# Revit family: Grohe_TowelHolder_Selection_41219KF0
name_source: partatom
category: Plumbing Fixtures
units: mm (PartAtom-declared; Revit-internal decimal feet)

## family parameters
Cut with Voids When Loaded = No
Host = Face
OmniClass Number = 23.45.05.00
OmniClass Title = Sanitary Equipment
Part Type = Normal
Room Calculation Point = No
Round Connector Dimension = Use Diameter
Shared = No

## types (1)
- SELECTION Towel Holder (41219KF0)
    Assembly Code = D2010
    AssetType = Fixed
    BIMObjectName = Grohe_TowelHolder_Selection_41219KF0
    CO2NeutralProduction = GROHE is one of the first leading manufacturer within the sanitary industry having a CO2-neutral production.
    CW Connection = No
    ClassificationName = Uniclass2015
    ClassificationValue = Pr_40_20_76_90
    Color = Matt Black
    Cost = 0 $
    Default Elevation = 0 mm  [stored 0 ft]
    Description = SELECTION Towel Holder
    DimensionsDocumentLink = https://cdn.cloud.grohe.com
    DocumentationCertificates = https://www.bimstore.co
    DocumentationInstallationGuide = https://www.bimstore.co
    DocumentationLiterature = https://www.bimstore.co
    DocumentationMaintenance = https://www.bimstore.co
    DocumentationTechnical = https://www.bimstore.co
    DurationUnit = Years
    EF000003 = Wall
    EF000007 = Black
    EF000040 = 30 mm  [stored 0.0984252 ft]
    EF000049 = 441 mm  [stored 1.44685 ft]
    EF000051 = Rack/bracket
    EF000139 = Lacquered
    EF000301 = TRUE
    EF000329 = FALSE
    EF000551 = 0 mm  [stored 0 ft]
    EF001438 = 0 mm  [stored 0 ft]
    EF002169 = Other
    EF006009 = TRUE
    EF011628 = FALSE
    EF022116 = Flat rod
    EF022280 = TRUE
    EF023686 = Other
    EF023790 = FALSE
    EF024007 = 2
    EF024009 = FALSE
    EF024463 = Round
    EF024489 = FALSE
    EF025109 = Other
    EF025110 = 0
    Ecojoy = No
    ExpectedLife = 0
    FullRecyclabilityOfPlastic = All plastic components are fully recyclable
    GROHESocialCommittment = green.grohe.com/social_engagement
    GROHESustainability = green.grohe.com
    HW Connection = No
    IfcExportAs = IfcPipeFitting
    IfcExportType = IfcPipeFittingType
    Keynote = N13
    Manufacturer = Grohe
    ManufacturerName = Grohe
    Model = SELECTION Towel Holder
    ModelNumber = 41219KF0
    ModelReference = SELECTION Towel Holder
    NBSDescription = Towel rails
    NBSObjectName = Grohe - Towel rails
    NBSReference = 45-35-72/372
    NominalDepth = 0 mm  [stored 0 ft]
    NominalHeight = 0 mm  [stored 0 ft]
    NominalLength = 0 mm  [stored 0 ft]
    PrimaryMaterial = Grohe_MattBlack
    ProductDescription = material: metal

depth 441 mm (functional depth 400 mm)

two arms

concealed fastening

GROHE Long-Life Shine finish
    ProductNumber = 41219KF0
    ProductPageURL = https://www.grohe.co.uk
    ProductShortText = Towel holder, pivotable
    ProductType = Accessory Bath
    ProductionYear = 2023
    SustainabilityAward = green.grohe.com/awards
    SustainabilityReport = green.grohe.com/reporting
    TPIDocumentLink = https://cdn.cloud.grohe.com
    Type Comments = SELECTION Towel Holder
    TypeName = SELECTION Towel Holder
    URL = https://www.grohe.co.uk
    Vent Connection = No
    WarrantyDurationLabor = 0
    WarrantyDurationParts = 0
    WarrantyDurationUnit = Years
    Waste Connection = No
    _BSBibleVersion = 17
    _BimSpecGuid = 0
    _CurrentRevision = 1
    _DistributedBy = https://www.bimstore.co
    _ObjectUserGuide = https://www.bimstore.co

note: [stored X ft] marks values corroborated as IEEE doubles in the binary element streams (Revit-internal decimal feet)

## geometry (parser evidence)
native form markers: Sweep x2
no freeform markers — native parametric forms only
